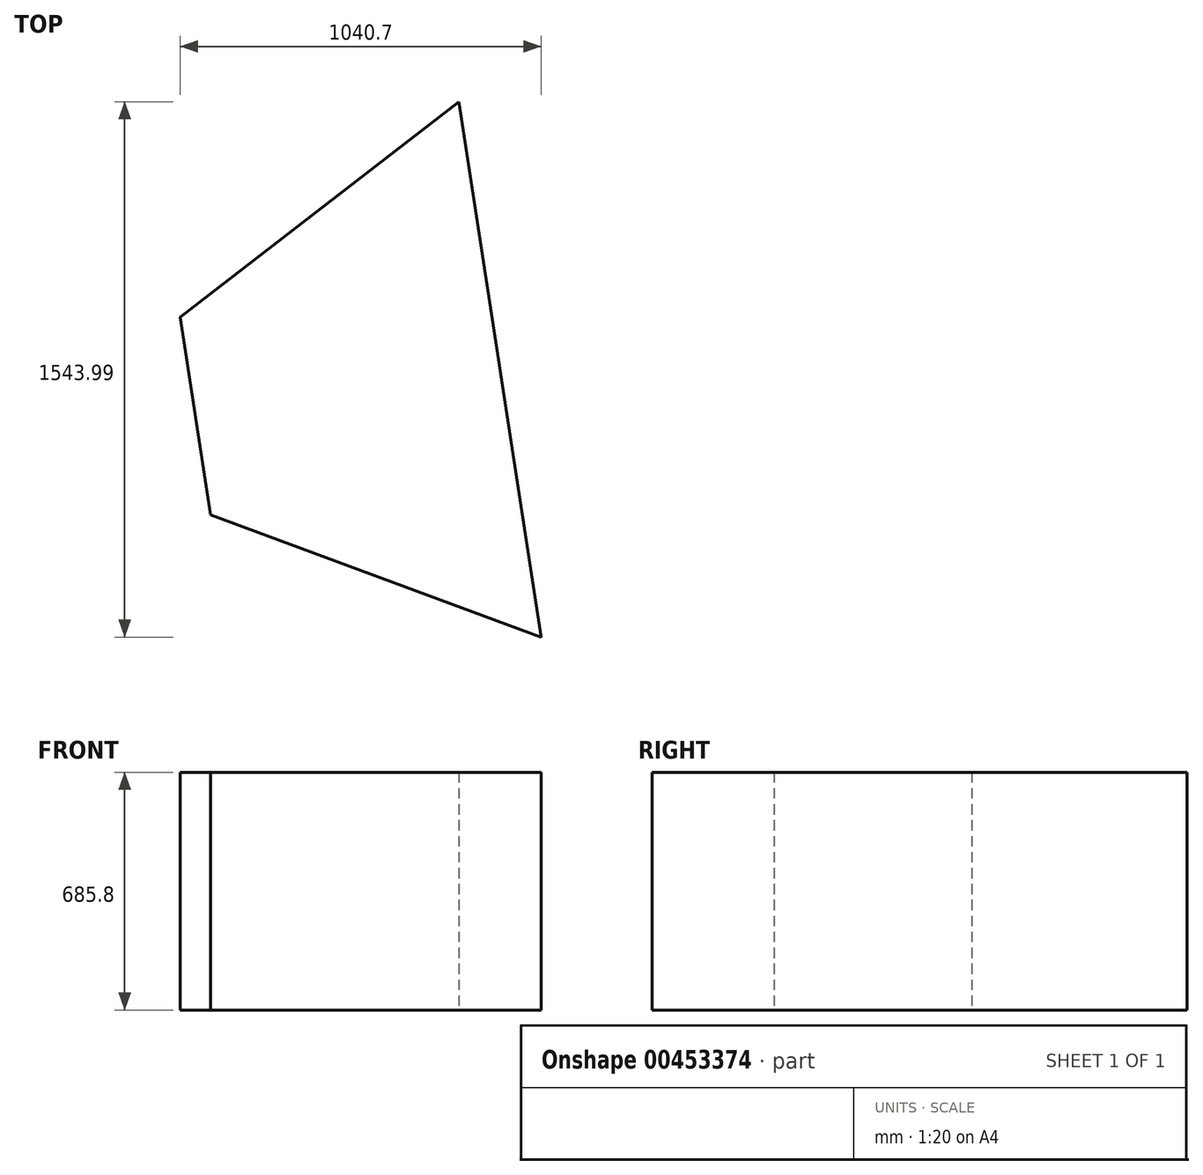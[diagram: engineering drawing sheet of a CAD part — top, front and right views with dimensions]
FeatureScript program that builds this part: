
annotation { "Feature Type Name" : "Feature", "Feature Type Description" : "" }
export const myFeature = defineFeature(function(context is Context, id is Id, definition is map)
    precondition{}
    {
        {
            var Q0;
            Q0=qCreatedBy(makeId("Top.planeOp"),FACE);
            var sketch = newSketch(context, id + "F0", { "sketchPlane" : qUnion([Q0])});
            skLineSegment(sketch, "E0", {"start": v(661.33, 1212.37) * mm, "end": v(898.52, -331.62) * mm});
            skLineSegment(sketch, "E1", {"start": v(898.52, -331.62) * mm, "end": v(-54.58, 20.31) * mm});
            skLineSegment(sketch, "E2", {"start": v(661.33, 1212.37) * mm, "end": v(-142.18, 590.59) * mm});
            skLineSegment(sketch, "E3", {"start": v(-142.18, 590.59) * mm, "end": v(-54.58, 20.31) * mm});
            skSolve(sketch);
        }
        {
            var Q0;
            Q0 = qSketchRegion(id + "F0", true);
            extrude(context, id + "F1", {"entities" : qUnion([Q0]), "depth" : 685.8 * mm});
        }
    });
